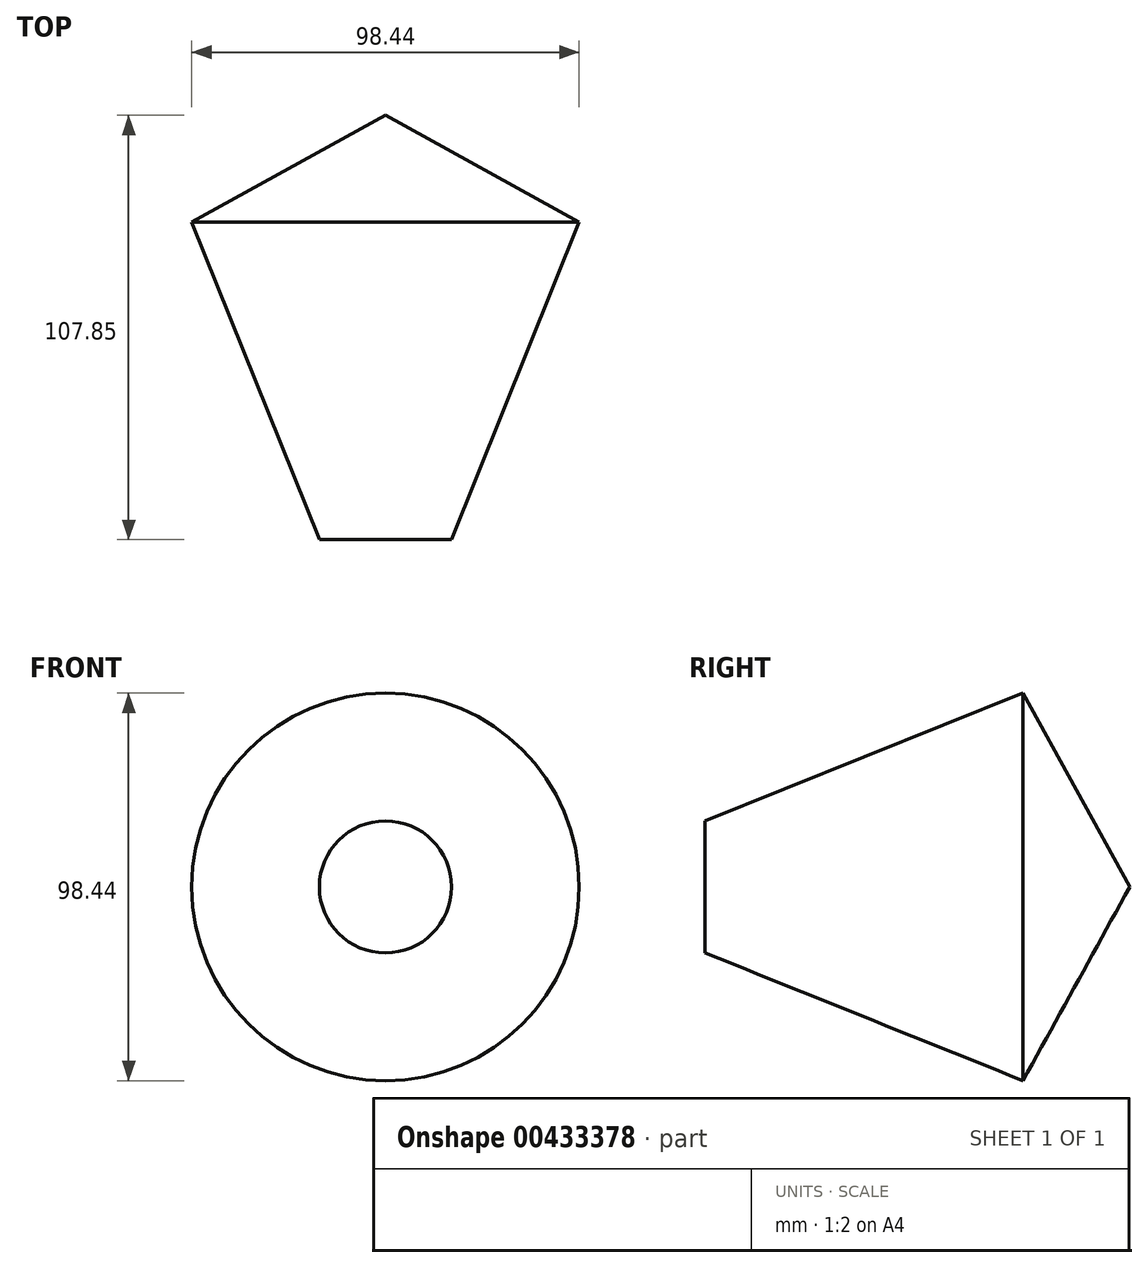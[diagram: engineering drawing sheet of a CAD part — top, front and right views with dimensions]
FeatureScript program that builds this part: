
annotation { "Feature Type Name" : "Feature", "Feature Type Description" : "" }
export const myFeature = defineFeature(function(context is Context, id is Id, definition is map)
    precondition{}
    {
        {
            var Q0;
            Q0=qCreatedBy(makeId("Top.planeOp"),FACE);
            var sketch = newSketch(context, id + "F0", { "sketchPlane" : qUnion([Q0])});
            skLineSegment(sketch, "E0", {"start": v(0, 37.06) * mm, "end": v(-49.22, 9.96) * mm});
            skLineSegment(sketch, "E1", {"start": v(-49.22, 9.96) * mm, "end": v(-16.78, -70.8) * mm});
            skLineSegment(sketch, "E2", {"start": v(-16.78, -70.8) * mm, "end": v(0, -70.8) * mm});
            skLineSegment(sketch, "E3", {"start": v(0, -70.8) * mm, "end": v(0, 37.06) * mm});
            skSolve(sketch);
        }
        {
            var Q0;
            Q0=makeQuery(id+"F0.imprint","IMPRINT",FACE,{"disambiguationData":[TD([[makeQuery(id+"F0.imprint","IMPRINT",EDGE,{"derivedFrom":sQuery(id+"F0.wireOp",EDGE,"E0")}),1.0]])]});
            var Q1;
            Q1=sQuery(id+"F0.wireOp",EDGE,"E3");
            revolve(context, id + "F1", {"entities" : qUnion([Q0]), "axis" : qUnion([Q1]), "revolveType" : RevolveType.FULL});
        }
    });
